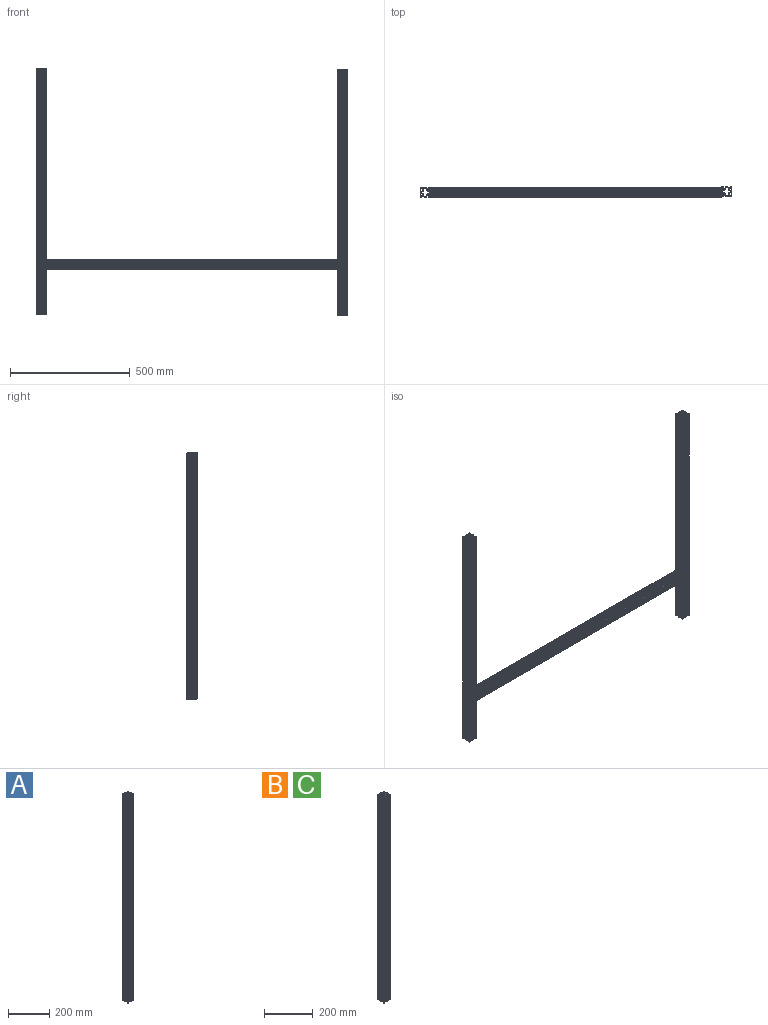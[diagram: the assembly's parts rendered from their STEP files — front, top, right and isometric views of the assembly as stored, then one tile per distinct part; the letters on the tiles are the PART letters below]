
ASSEMBLY  parts=3 mates=2
PART A: 186 faces, bbox 40x40x1220 mm
  f0: plane 1220x1.64mm, normal (0,1,0), area 2000mm2, adj f1,f183,f184,f185
  f1: plane 1220x3.06mm, normal (0.71,0.71,0), area 5280.7mm2, adj f0,f2,f184,f185
  f2: plane 1220x1.95mm, normal (1,0,0), area 2375.6mm2, adj f1,f3,f184,f185
  f3: plane 1220x0.49mm, normal (0.83,0.56,0), area 724.2mm2, adj f2,f4,f184,f185
  f4: plane 1220x0.62mm, normal (0.88,-0.47,0), area 862.7mm2, adj f3,f5,f184,f185
  f5: plane 1220x1.95mm, normal (1,0,0), area 2375.6mm2, adj f4,f6,f184,f185
  f6: plane 1220x3.06mm, normal (0.69,-0.72,0), area 5167.9mm2, adj f5,f7,f184,f185
  f7: plane 1220x1.64mm, normal (0,-1,0), area 2000mm2, adj f6,f8,f184,f185
  f8: plane 1220x2.39mm, normal (-1,0,0), area 2909.7mm2, adj f7,f9,f184,f185
  f9: plane 1220x1.8mm, normal (0.71,-0.71,0), area 3105.6mm2, adj f8,f10,f184,f185
  f10: plane 1220x3.71mm, normal (1,0,0), area 4527.3mm2, adj f9,f11,f184,f185
  f11: cylinder r=1.59mm len=1220mm, axis (0,0,-1), area 4048.6mm2, adj f10,f12,f184,f185
  f12: plane 1220x3.71mm, normal (1,0,0), area 4527.3mm2, adj f11,f13,f184,f185
  f13: plane 1220x1.8mm, normal (0.71,0.71,0), area 3105.6mm2, adj f12,f14,f184,f185
  f14: plane 1220x2.39mm, normal (-1,0,0), area 2909.7mm2, adj f13,f15,f184,f185
  f15: plane 1220x1.64mm, normal (0,1,0), area 2000mm2, adj f14,f16,f184,f185
  f16: plane 1220x3.06mm, normal (0.69,0.72,0), area 5167.9mm2, adj f15,f17,f184,f185
  f17: plane 1220x1.95mm, normal (1,0,0), area 2375.6mm2, adj f16,f18,f184,f185
  f18: plane 1220x0.62mm, normal (0.88,0.47,0), area 862.7mm2, adj f17,f19,f184,f185
  f19: plane 1220x0.49mm, normal (0.83,-0.56,0), area 724.2mm2, adj f18,f20,f184,f185
  f20: plane 1220x1.95mm, normal (1,0,0), area 2375.6mm2, adj f19,f21,f184,f185
  f21: plane 1220x3.06mm, normal (0.71,-0.71,0), area 5280.7mm2, adj f20,f22,f184,f185
  f22: plane 1220x1.64mm, normal (0,-1,0), area 2000mm2, adj f21,f23,f184,f185
  f23: plane 1220x2.39mm, normal (-1,0,0), area 2909.7mm2, adj f22,f24,f184,f185
  f24: plane 1220x1.8mm, normal (0.71,-0.71,0), area 3105.6mm2, adj f23,f25,f184,f185
  f25: plane 1220x1.16mm, normal (1,0,0), area 1416.3mm2, adj f24,f26,f184,f185
  f26: cylinder r=1.59mm len=1220mm, axis (0,0,-1), area 4048.6mm2, adj f25,f27,f184,f185
  f27: plane 1220x0.68mm, normal (1,0,0), area 824.6mm2, adj f26,f28,f184,f185
  f28: cylinder r=0.5mm len=1220mm, axis (0,0,-1), area 958.2mm2, adj f27,f29,f184,f185
  f29: plane 1220x0.68mm, normal (0,1,0), area 824.6mm2, adj f28,f30,f184,f185
  f30: cylinder r=1.59mm len=1220mm, axis (0,0,-1), area 4048.6mm2, adj f29,f31,f184,f185
  f31: plane 1220x1.16mm, normal (0,1,0), area 1416.3mm2, adj f30,f32,f184,f185
  f32: plane 1220x1.8mm, normal (-0.71,0.71,0), area 3105.6mm2, adj f31,f33,f184,f185
  f33: plane 1220x2.39mm, normal (0,-1,0), area 2909.7mm2, adj f32,f34,f184,f185
  f34: plane 1220x1.64mm, normal (-1,0,0), area 2000mm2, adj f33,f35,f184,f185
  f35: plane 1220x3.06mm, normal (-0.71,0.71,0), area 5280.7mm2, adj f34,f36,f184,f185
  f36: plane 1220x1.95mm, normal (0,1,0), area 2375.6mm2, adj f35,f37,f184,f185
  f37: plane 1220x0.49mm, normal (-0.52,0.86,0), area 700.5mm2, adj f36,f38,f184,f185
  f38: plane 1220x0.49mm, normal (0.52,0.86,0), area 700.5mm2, adj f37,f39,f184,f185
  f39: plane 1220x1.95mm, normal (0,1,0), area 2375.6mm2, adj f38,f40,f184,f185
  f40: plane 1220x3.06mm, normal (0.71,0.71,0), area 5280.7mm2, adj f39,f41,f184,f185
  f41: plane 1220x1.64mm, normal (1,0,0), area 2000mm2, adj f40,f42,f184,f185
  f42: plane 1220x2.39mm, normal (0,-1,0), area 2909.7mm2, adj f41,f43,f184,f185
  f43: plane 1220x1.8mm, normal (0.71,0.71,0), area 3105.6mm2, adj f42,f44,f184,f185
  f44: plane 1220x3.71mm, normal (0,1,0), area 4527.3mm2, adj f43,f45,f184,f185
  f45: cylinder r=1.59mm len=1220mm, axis (0,0,-1), area 4048.6mm2, adj f44,f46,f184,f185
  f46: plane 1220x3.71mm, normal (0,1,0), area 4527.3mm2, adj f45,f47,f184,f185
  f47: plane 1220x1.8mm, normal (-0.71,0.71,0), area 3105.6mm2, adj f46,f48,f184,f185
  f48: plane 1220x2.39mm, normal (0,-1,0), area 2909.7mm2, adj f47,f49,f184,f185
  f49: plane 1220x1.64mm, normal (-1,0,0), area 2000mm2, adj f48,f50,f184,f185
  f50: plane 1220x3.06mm, normal (-0.71,0.71,0), area 5280.7mm2, adj f49,f51,f184,f185
  f51: plane 1220x1.95mm, normal (0,1,0), area 2375.6mm2, adj f50,f52,f184,f185
  f52: plane 1220x0.49mm, normal (-0.52,0.86,0), area 700.5mm2, adj f51,f53,f184,f185
  f53: plane 1220x0.49mm, normal (0.52,0.86,0), area 700.5mm2, adj f52,f54,f184,f185
  f54: plane 1220x1.95mm, normal (0,1,0), area 2375.6mm2, adj f53,f55,f184,f185
  f55: plane 1220x3.06mm, normal (0.71,0.71,0), area 5280.7mm2, adj f54,f56,f184,f185
  f56: plane 1220x1.64mm, normal (1,0,0), area 2000mm2, adj f55,f57,f184,f185
  f57: plane 1220x2.39mm, normal (0,-1,0), area 2909.7mm2, adj f56,f58,f184,f185
  f58: plane 1220x1.8mm, normal (0.71,0.71,0), area 3105.6mm2, adj f57,f59,f184,f185
  f59: plane 1220x1.16mm, normal (0,1,0), area 1416.3mm2, adj f58,f60,f184,f185
  f60: cylinder r=1.59mm len=1220mm, axis (0,0,-1), area 4048.6mm2, adj f59,f61,f184,f185
  f61: plane 1220x0.68mm, normal (0,1,0), area 824.6mm2, adj f60,f62,f184,f185
  f62: cylinder r=0.5mm len=1220mm, axis (0,0,-1), area 958.2mm2, adj f61,f63,f184,f185
  f63: plane 1220x0.68mm, normal (-1,0,0), area 824.6mm2, adj f62,f64,f184,f185
  f64: cylinder r=1.59mm len=1220mm, axis (0,0,-1), area 4048.6mm2, adj f63,f65,f184,f185
  f65: plane 1220x1.16mm, normal (-1,0,0), area 1416.3mm2, adj f64,f66,f184,f185
  f66: plane 1220x1.8mm, normal (-0.71,-0.71,0), area 3105.6mm2, adj f65,f67,f184,f185
  f67: plane 1220x2.39mm, normal (1,0,0), area 2909.7mm2, adj f66,f68,f184,f185
  f68: plane 1220x1.64mm, normal (0,-1,0), area 2000mm2, adj f67,f69,f184,f185
  f69: plane 1220x3.06mm, normal (-0.71,-0.71,0), area 5280.7mm2, adj f68,f70,f184,f185
  f70: plane 1220x1.95mm, normal (-1,0,0), area 2375.6mm2, adj f69,f71,f184,f185
  f71: plane 1220x0.49mm, normal (-0.83,-0.56,0), area 724.2mm2, adj f70,f72,f184,f185
  f72: plane 1220x0.62mm, normal (-0.88,0.47,0), area 862.7mm2, adj f71,f73,f184,f185
  f73: plane 1220x1.95mm, normal (-1,0,0), area 2375.6mm2, adj f72,f74,f184,f185
  f74: plane 1220x3.06mm, normal (-0.69,0.72,0), area 5167.9mm2, adj f73,f75,f184,f185
  f75: plane 1220x1.64mm, normal (0,1,0), area 2000mm2, adj f74,f76,f184,f185
  f76: plane 1220x2.39mm, normal (1,0,0), area 2909.7mm2, adj f75,f77,f184,f185
  f77: plane 1220x1.8mm, normal (-0.71,0.71,0), area 3105.6mm2, adj f76,f78,f184,f185
  f78: plane 1220x3.71mm, normal (-1,0,0), area 4527.3mm2, adj f77,f79,f184,f185
  f79: cylinder r=1.59mm len=1220mm, axis (0,0,-1), area 4048.6mm2, adj f78,f80,f184,f185
  f80: plane 1220x3.71mm, normal (-1,0,0), area 4527.3mm2, adj f79,f81,f184,f185
  f81: plane 1220x1.8mm, normal (-0.71,-0.71,0), area 3105.6mm2, adj f80,f82,f184,f185
  f82: plane 1220x2.39mm, normal (1,0,0), area 2909.7mm2, adj f81,f83,f184,f185
  f83: plane 1220x1.64mm, normal (0,-1,0), area 2000mm2, adj f82,f84,f184,f185
  f84: plane 1220x3.06mm, normal (-0.69,-0.72,0), area 5167.9mm2, adj f83,f85,f184,f185
  f85: plane 1220x1.95mm, normal (-1,0,0), area 2375.6mm2, adj f84,f86,f184,f185
  f86: plane 1220x0.62mm, normal (-0.88,-0.47,0), area 862.7mm2, adj f85,f87,f184,f185
  f87: plane 1220x0.49mm, normal (-0.83,0.56,0), area 724.2mm2, adj f86,f88,f184,f185
  f88: plane 1220x1.95mm, normal (-1,0,0), area 2375.6mm2, adj f87,f89,f184,f185
  f89: plane 1220x3.06mm, normal (-0.71,0.71,0), area 5280.7mm2, adj f88,f90,f184,f185
  f90: plane 1220x1.64mm, normal (0,1,0), area 2000mm2, adj f89,f91,f184,f185
  f91: plane 1220x2.39mm, normal (1,0,0), area 2909.7mm2, adj f90,f92,f184,f185
  f92: plane 1220x1.8mm, normal (-0.71,0.71,0), area 3105.6mm2, adj f91,f93,f184,f185
  f93: plane 1220x1.16mm, normal (-1,0,0), area 1416.3mm2, adj f92,f94,f184,f185
  f94: cylinder r=1.59mm len=1220mm, axis (0,0,-1), area 4048.6mm2, adj f93,f95,f184,f185
  f95: plane 1220x0.68mm, normal (-1,0,0), area 824.6mm2, adj f94,f96,f184,f185
  f96: cylinder r=0.5mm len=1220mm, axis (0,0,-1), area 958.2mm2, adj f95,f97,f184,f185
  f97: plane 1220x0.68mm, normal (0,-1,0), area 824.6mm2, adj f96,f98,f184,f185
  f98: cylinder r=1.59mm len=1220mm, axis (0,0,-1), area 4048.6mm2, adj f97,f99,f184,f185
  f99: plane 1220x1.16mm, normal (0,-1,0), area 1416.3mm2, adj f98,f100,f184,f185
  f100: plane 1220x1.8mm, normal (0.71,-0.71,0), area 3105.6mm2, adj f99,f101,f184,f185
  f101: plane 1220x2.39mm, normal (0,1,0), area 2909.7mm2, adj f100,f102,f184,f185
  f102: plane 1220x1.64mm, normal (1,0,0), area 2000mm2, adj f101,f103,f184,f185
  f103: plane 1220x3.06mm, normal (0.71,-0.71,0), area 5280.7mm2, adj f102,f104,f184,f185
  f104: plane 1220x1.95mm, normal (0,-1,0), area 2375.6mm2, adj f103,f105,f184,f185
  f105: plane 1220x0.49mm, normal (0.52,-0.86,0), area 700.5mm2, adj f104,f106,f184,f185
  f106: plane 1220x0.49mm, normal (-0.52,-0.86,0), area 700.5mm2, adj f105,f107,f184,f185
  f107: plane 1220x1.95mm, normal (0,-1,0), area 2375.6mm2, adj f106,f108,f184,f185
  f108: plane 1220x3.06mm, normal (-0.71,-0.71,0), area 5280.7mm2, adj f107,f109,f184,f185
  f109: plane 1220x1.64mm, normal (-1,0,0), area 2000mm2, adj f108,f110,f184,f185
  f110: plane 1220x2.39mm, normal (0,1,0), area 2909.7mm2, adj f109,f111,f184,f185
  f111: plane 1220x1.8mm, normal (-0.71,-0.71,0), area 3105.6mm2, adj f110,f112,f184,f185
  f112: plane 1220x3.71mm, normal (0,-1,0), area 4527.3mm2, adj f111,f113,f184,f185
  f113: cylinder r=1.59mm len=1220mm, axis (0,0,-1), area 4048.6mm2, adj f112,f114,f184,f185
  f114: plane 1220x3.71mm, normal (0,-1,0), area 4527.3mm2, adj f113,f115,f184,f185
  f115: plane 1220x1.8mm, normal (0.71,-0.71,0), area 3105.6mm2, adj f114,f116,f184,f185
  f116: plane 1220x2.39mm, normal (0,1,0), area 2909.7mm2, adj f115,f117,f184,f185
  f117: plane 1220x1.64mm, normal (1,0,0), area 2000mm2, adj f116,f118,f184,f185
  f118: plane 1220x3.06mm, normal (0.71,-0.71,0), area 5280.7mm2, adj f117,f119,f184,f185
  f119: plane 1220x1.95mm, normal (0,-1,0), area 2375.6mm2, adj f118,f120,f184,f185
  f120: plane 1220x0.49mm, normal (0.52,-0.86,0), area 700.5mm2, adj f119,f121,f184,f185
  f121: plane 1220x0.49mm, normal (-0.52,-0.86,0), area 700.5mm2, adj f120,f122,f184,f185
  f122: plane 1220x1.95mm, normal (0,-1,0), area 2375.6mm2, adj f121,f123,f184,f185
  f123: plane 1220x3.06mm, normal (-0.71,-0.71,0), area 5280.7mm2, adj f122,f124,f184,f185
  f124: plane 1220x1.64mm, normal (-1,0,0), area 2000mm2, adj f123,f125,f184,f185
  f125: plane 1220x2.39mm, normal (0,1,0), area 2909.7mm2, adj f124,f126,f184,f185
  f126: plane 1220x1.8mm, normal (-0.71,-0.71,0), area 3105.6mm2, adj f125,f127,f184,f185
  f127: plane 1220x1.16mm, normal (0,-1,0), area 1416.3mm2, adj f126,f128,f184,f185
  f128: cylinder r=1.59mm len=1220mm, axis (0,0,-1), area 4048.6mm2, adj f127,f129,f184,f185
  f129: plane 1220x0.68mm, normal (0,-1,0), area 824.6mm2, adj f128,f130,f184,f185
  f130: cylinder r=0.5mm len=1220mm, axis (0,0,-1), area 958.2mm2, adj f129,f131,f184,f185
  f131: plane 1220x0.68mm, normal (1,0,0), area 824.6mm2, adj f130,f132,f184,f185
  f132: cylinder r=1.59mm len=1220mm, axis (0,0,-1), area 4048.6mm2, adj f131,f133,f184,f185
  f133: plane 1220x1.16mm, normal (1,0,0), area 1416.3mm2, adj f132,f134,f184,f185
  f134: plane 1220x1.8mm, normal (0.71,0.71,0), area 3105.6mm2, adj f133,f183,f184,f185
  f135: cylinder r=2.1mm len=1220mm, axis (0,0,-1), area 14264.2mm2, adj f136,f182,f184,f185
  f136: plane 1220x1.59mm, normal (0,1,0), area 1938.7mm2, adj f135,f137,f184,f185
  f137: plane 1220x3.31mm, normal (-1,0,0), area 4038.4mm2, adj f136,f138,f184,f185
  f138: plane 1220x3.8mm, normal (-0.71,0.71,0), area 6556.3mm2, adj f137,f139,f184,f185
  f139: plane 1220x1.96mm, normal (-1,0,0), area 2392mm2, adj f138,f140,f184,f185
  f140: plane 1220x0.52mm, normal (0,1,0), area 640.1mm2, adj f139,f141,f184,f185
  f141: cylinder r=3.39mm len=1220mm, axis (0,0,-1), area 5762.9mm2, adj f140,f142,f184,f185
  f142: plane 1220x0.52mm, normal (0,1,0), area 640.1mm2, adj f141,f143,f184,f185
  f143: plane 1220x1.96mm, normal (1,0,0), area 2392mm2, adj f142,f144,f184,f185
  f144: plane 1220x3.8mm, normal (0.71,0.71,0), area 6556.3mm2, adj f143,f145,f184,f185
  f145: plane 1220x3.31mm, normal (1,0,0), area 4038.4mm2, adj f144,f146,f184,f185
  f146: plane 1220x1.59mm, normal (0,1,0), area 1938.7mm2, adj f145,f147,f184,f185
  f147: cylinder r=2.1mm len=1220mm, axis (0,0,-1), area 14264.2mm2, adj f146,f148,f184,f185
  f148: plane 1220x1.59mm, normal (1,0,0), area 1938.7mm2, adj f147,f149,f184,f185
  f149: plane 1220x3.17mm, normal (0,1,0), area 3869.3mm2, adj f148,f150,f184,f185
  f150: plane 1220x3.97mm, normal (0.69,0.72,0), area 6705.9mm2, adj f149,f151,f184,f185
  f151: plane 1220x1.93mm, normal (0,1,0), area 2351.9mm2, adj f150,f152,f184,f185
  f152: plane 1220x0.52mm, normal (1,0,0), area 640.1mm2, adj f151,f153,f184,f185
  f153: cylinder r=3.39mm len=1220mm, axis (0,0,-1), area 5762.9mm2, adj f152,f154,f184,f185
  f154: plane 1220x0.52mm, normal (1,0,0), area 640.1mm2, adj f153,f155,f184,f185
  f155: plane 1220x1.93mm, normal (0,-1,0), area 2351.9mm2, adj f154,f156,f184,f185
  f156: plane 1220x3.97mm, normal (0.69,-0.72,0), area 6705.9mm2, adj f155,f157,f184,f185
  f157: plane 1220x3.17mm, normal (0,-1,0), area 3869.3mm2, adj f156,f158,f184,f185
  f158: plane 1220x1.59mm, normal (1,0,0), area 1938.7mm2, adj f157,f159,f184,f185
  f159: cylinder r=2.1mm len=1220mm, axis (0,0,-1), area 14264.2mm2, adj f158,f160,f184,f185
  f160: plane 1220x1.59mm, normal (0,-1,0), area 1938.7mm2, adj f159,f161,f184,f185
  f161: plane 1220x3.31mm, normal (1,0,0), area 4038.4mm2, adj f160,f162,f184,f185
  f162: plane 1220x3.8mm, normal (0.71,-0.71,0), area 6556.3mm2, adj f161,f163,f184,f185
  f163: plane 1220x1.96mm, normal (1,0,0), area 2392mm2, adj f162,f164,f184,f185
  f164: plane 1220x0.52mm, normal (0,-1,0), area 640.1mm2, adj f163,f165,f184,f185
  f165: cylinder r=3.39mm len=1220mm, axis (0,0,-1), area 5762.9mm2, adj f164,f166,f184,f185
  f166: plane 1220x0.52mm, normal (0,-1,0), area 640.1mm2, adj f165,f167,f184,f185
  f167: plane 1220x1.96mm, normal (-1,0,0), area 2392mm2, adj f166,f168,f184,f185
  f168: plane 1220x3.8mm, normal (-0.71,-0.71,0), area 6556.3mm2, adj f167,f169,f184,f185
  f169: plane 1220x3.31mm, normal (-1,0,0), area 4038.4mm2, adj f168,f170,f184,f185
  f170: plane 1220x1.59mm, normal (0,-1,0), area 1938.7mm2, adj f169,f171,f184,f185
  f171: cylinder r=2.1mm len=1220mm, axis (0,0,-1), area 14264.2mm2, adj f170,f172,f184,f185
  f172: plane 1220x1.59mm, normal (-1,0,0), area 1938.7mm2, adj f171,f173,f184,f185
  f173: plane 1220x3.17mm, normal (0,-1,0), area 3869.3mm2, adj f172,f174,f184,f185
  f174: plane 1220x3.97mm, normal (-0.69,-0.72,0), area 6705.9mm2, adj f173,f175,f184,f185
  f175: plane 1220x1.93mm, normal (0,-1,0), area 2351.9mm2, adj f174,f176,f184,f185
  f176: plane 1220x0.52mm, normal (-1,0,0), area 640.1mm2, adj f175,f177,f184,f185
  f177: cylinder r=3.39mm len=1220mm, axis (0,0,-1), area 5762.9mm2, adj f176,f178,f184,f185
  f178: plane 1220x0.52mm, normal (-1,0,0), area 640.1mm2, adj f177,f179,f184,f185
  f179: plane 1220x1.93mm, normal (0,1,0), area 2351.9mm2, adj f178,f180,f184,f185
  f180: plane 1220x3.97mm, normal (-0.69,0.72,0), area 6705.9mm2, adj f179,f181,f184,f185
  f181: plane 1220x3.17mm, normal (0,1,0), area 3869.3mm2, adj f180,f182,f184,f185
  f182: plane 1220x1.59mm, normal (-1,0,0), area 1938.7mm2, adj f135,f181,f184,f185
  f183: plane 1220x2.39mm, normal (-1,0,0), area 2909.7mm2, adj f0,f134,f184,f185
  f184: plane 40x40mm, normal (0,0,1), area 394.7mm2, adj f0,f1,f2,f3,f4,f5,f6,f7
  f185: plane 40x40mm, normal (0,0,-1), area 394.7mm2, adj f0,f1,f2,f3,f4,f5,f6,f7
PART B: 186 faces, bbox 40x40x1030 mm
  f0: plane 1030x1.64mm, normal (0,1,0), area 1688.5mm2, adj f1,f183,f184,f185
  f1: plane 1030x3.06mm, normal (0.71,0.71,0), area 4458.3mm2, adj f0,f2,f184,f185
  f2: plane 1030x1.95mm, normal (1,0,0), area 2005.6mm2, adj f1,f3,f184,f185
  f3: plane 1030x0.49mm, normal (0.83,0.56,0), area 611.5mm2, adj f2,f4,f184,f185
  f4: plane 1030x0.62mm, normal (0.88,-0.47,0), area 728.3mm2, adj f3,f5,f184,f185
  f5: plane 1030x1.95mm, normal (1,0,0), area 2005.6mm2, adj f4,f6,f184,f185
  f6: plane 1030x3.06mm, normal (0.69,-0.72,0), area 4363.1mm2, adj f5,f7,f184,f185
  f7: plane 1030x1.64mm, normal (0,-1,0), area 1688.5mm2, adj f6,f8,f184,f185
  f8: plane 1030x2.39mm, normal (-1,0,0), area 2456.6mm2, adj f7,f9,f184,f185
  f9: plane 1030x1.8mm, normal (0.71,-0.71,0), area 2622mm2, adj f8,f10,f184,f185
  f10: plane 1030x3.71mm, normal (1,0,0), area 3822.2mm2, adj f9,f11,f184,f185
  f11: cylinder r=1.59mm len=1030mm, axis (0,0,-1), area 3418.1mm2, adj f10,f12,f184,f185
  f12: plane 1030x3.71mm, normal (1,0,0), area 3822.2mm2, adj f11,f13,f184,f185
  f13: plane 1030x1.8mm, normal (0.71,0.71,0), area 2622mm2, adj f12,f14,f184,f185
  f14: plane 1030x2.39mm, normal (-1,0,0), area 2456.5mm2, adj f13,f15,f184,f185
  f15: plane 1030x1.64mm, normal (0,1,0), area 1688.5mm2, adj f14,f16,f184,f185
  f16: plane 1030x3.06mm, normal (0.69,0.72,0), area 4363.1mm2, adj f15,f17,f184,f185
  f17: plane 1030x1.95mm, normal (1,0,0), area 2005.6mm2, adj f16,f18,f184,f185
  f18: plane 1030x0.62mm, normal (0.88,0.47,0), area 728.3mm2, adj f17,f19,f184,f185
  f19: plane 1030x0.49mm, normal (0.83,-0.56,0), area 611.5mm2, adj f18,f20,f184,f185
  f20: plane 1030x1.95mm, normal (1,0,0), area 2005.6mm2, adj f19,f21,f184,f185
  f21: plane 1030x3.06mm, normal (0.71,-0.71,0), area 4458.3mm2, adj f20,f22,f184,f185
  f22: plane 1030x1.64mm, normal (0,-1,0), area 1688.5mm2, adj f21,f23,f184,f185
  f23: plane 1030x2.39mm, normal (-1,0,0), area 2456.6mm2, adj f22,f24,f184,f185
  f24: plane 1030x1.8mm, normal (0.71,-0.71,0), area 2622mm2, adj f23,f25,f184,f185
  f25: plane 1030x1.16mm, normal (1,0,0), area 1195.7mm2, adj f24,f26,f184,f185
  f26: cylinder r=1.59mm len=1030mm, axis (0,0,-1), area 3418.1mm2, adj f25,f27,f184,f185
  f27: plane 1030x0.68mm, normal (1,0,0), area 696.2mm2, adj f26,f28,f184,f185
  f28: cylinder r=0.5mm len=1030mm, axis (0,0,-1), area 809mm2, adj f27,f29,f184,f185
  f29: plane 1030x0.68mm, normal (0,1,0), area 696.2mm2, adj f28,f30,f184,f185
  f30: cylinder r=1.59mm len=1030mm, axis (0,0,-1), area 3418.1mm2, adj f29,f31,f184,f185
  f31: plane 1030x1.16mm, normal (0,1,0), area 1195.7mm2, adj f30,f32,f184,f185
  f32: plane 1030x1.8mm, normal (-0.71,0.71,0), area 2622mm2, adj f31,f33,f184,f185
  f33: plane 1030x2.39mm, normal (0,-1,0), area 2456.5mm2, adj f32,f34,f184,f185
  f34: plane 1030x1.64mm, normal (-1,0,0), area 1688.5mm2, adj f33,f35,f184,f185
  f35: plane 1030x3.06mm, normal (-0.71,0.71,0), area 4458.3mm2, adj f34,f36,f184,f185
  f36: plane 1030x1.95mm, normal (0,1,0), area 2005.6mm2, adj f35,f37,f184,f185
  f37: plane 1030x0.49mm, normal (-0.52,0.86,0), area 591.4mm2, adj f36,f38,f184,f185
  f38: plane 1030x0.49mm, normal (0.52,0.86,0), area 591.4mm2, adj f37,f39,f184,f185
  f39: plane 1030x1.95mm, normal (0,1,0), area 2005.6mm2, adj f38,f40,f184,f185
  f40: plane 1030x3.06mm, normal (0.71,0.71,0), area 4458.3mm2, adj f39,f41,f184,f185
  f41: plane 1030x1.64mm, normal (1,0,0), area 1688.5mm2, adj f40,f42,f184,f185
  f42: plane 1030x2.39mm, normal (0,-1,0), area 2456.6mm2, adj f41,f43,f184,f185
  f43: plane 1030x1.8mm, normal (0.71,0.71,0), area 2622mm2, adj f42,f44,f184,f185
  f44: plane 1030x3.71mm, normal (0,1,0), area 3822.2mm2, adj f43,f45,f184,f185
  f45: cylinder r=1.59mm len=1030mm, axis (0,0,-1), area 3418.1mm2, adj f44,f46,f184,f185
  f46: plane 1030x3.71mm, normal (0,1,0), area 3822.2mm2, adj f45,f47,f184,f185
  f47: plane 1030x1.8mm, normal (-0.71,0.71,0), area 2622mm2, adj f46,f48,f184,f185
  f48: plane 1030x2.39mm, normal (0,-1,0), area 2456.6mm2, adj f47,f49,f184,f185
  f49: plane 1030x1.64mm, normal (-1,0,0), area 1688.5mm2, adj f48,f50,f184,f185
  f50: plane 1030x3.06mm, normal (-0.71,0.71,0), area 4458.3mm2, adj f49,f51,f184,f185
  f51: plane 1030x1.95mm, normal (0,1,0), area 2005.6mm2, adj f50,f52,f184,f185
  f52: plane 1030x0.49mm, normal (-0.52,0.86,0), area 591.4mm2, adj f51,f53,f184,f185
  f53: plane 1030x0.49mm, normal (0.52,0.86,0), area 591.4mm2, adj f52,f54,f184,f185
  f54: plane 1030x1.95mm, normal (0,1,0), area 2005.6mm2, adj f53,f55,f184,f185
  f55: plane 1030x3.06mm, normal (0.71,0.71,0), area 4458.3mm2, adj f54,f56,f184,f185
  f56: plane 1030x1.64mm, normal (1,0,0), area 1688.5mm2, adj f55,f57,f184,f185
  f57: plane 1030x2.39mm, normal (0,-1,0), area 2456.5mm2, adj f56,f58,f184,f185
  f58: plane 1030x1.8mm, normal (0.71,0.71,0), area 2622mm2, adj f57,f59,f184,f185
  f59: plane 1030x1.16mm, normal (0,1,0), area 1195.7mm2, adj f58,f60,f184,f185
  f60: cylinder r=1.59mm len=1030mm, axis (0,0,-1), area 3418.1mm2, adj f59,f61,f184,f185
  f61: plane 1030x0.68mm, normal (0,1,0), area 696.2mm2, adj f60,f62,f184,f185
  f62: cylinder r=0.5mm len=1030mm, axis (0,0,-1), area 809mm2, adj f61,f63,f184,f185
  f63: plane 1030x0.68mm, normal (-1,0,0), area 696.2mm2, adj f62,f64,f184,f185
  f64: cylinder r=1.59mm len=1030mm, axis (0,0,-1), area 3418.1mm2, adj f63,f65,f184,f185
  f65: plane 1030x1.16mm, normal (-1,0,0), area 1195.7mm2, adj f64,f66,f184,f185
  f66: plane 1030x1.8mm, normal (-0.71,-0.71,0), area 2622mm2, adj f65,f67,f184,f185
  f67: plane 1030x2.39mm, normal (1,0,0), area 2456.6mm2, adj f66,f68,f184,f185
  f68: plane 1030x1.64mm, normal (0,-1,0), area 1688.5mm2, adj f67,f69,f184,f185
  f69: plane 1030x3.06mm, normal (-0.71,-0.71,0), area 4458.3mm2, adj f68,f70,f184,f185
  f70: plane 1030x1.95mm, normal (-1,0,0), area 2005.6mm2, adj f69,f71,f184,f185
  f71: plane 1030x0.49mm, normal (-0.83,-0.56,0), area 611.5mm2, adj f70,f72,f184,f185
  f72: plane 1030x0.62mm, normal (-0.88,0.47,0), area 728.3mm2, adj f71,f73,f184,f185
  f73: plane 1030x1.95mm, normal (-1,0,0), area 2005.6mm2, adj f72,f74,f184,f185
  f74: plane 1030x3.06mm, normal (-0.69,0.72,0), area 4363.1mm2, adj f73,f75,f184,f185
  f75: plane 1030x1.64mm, normal (0,1,0), area 1688.5mm2, adj f74,f76,f184,f185
  f76: plane 1030x2.39mm, normal (1,0,0), area 2456.5mm2, adj f75,f77,f184,f185
  f77: plane 1030x1.8mm, normal (-0.71,0.71,0), area 2622mm2, adj f76,f78,f184,f185
  f78: plane 1030x3.71mm, normal (-1,0,0), area 3822.2mm2, adj f77,f79,f184,f185
  f79: cylinder r=1.59mm len=1030mm, axis (0,0,-1), area 3418.1mm2, adj f78,f80,f184,f185
  f80: plane 1030x3.71mm, normal (-1,0,0), area 3822.2mm2, adj f79,f81,f184,f185
  f81: plane 1030x1.8mm, normal (-0.71,-0.71,0), area 2622mm2, adj f80,f82,f184,f185
  f82: plane 1030x2.39mm, normal (1,0,0), area 2456.6mm2, adj f81,f83,f184,f185
  f83: plane 1030x1.64mm, normal (0,-1,0), area 1688.5mm2, adj f82,f84,f184,f185
  f84: plane 1030x3.06mm, normal (-0.69,-0.72,0), area 4363.1mm2, adj f83,f85,f184,f185
  f85: plane 1030x1.95mm, normal (-1,0,0), area 2005.6mm2, adj f84,f86,f184,f185
  f86: plane 1030x0.62mm, normal (-0.88,-0.47,0), area 728.3mm2, adj f85,f87,f184,f185
  f87: plane 1030x0.49mm, normal (-0.83,0.56,0), area 611.5mm2, adj f86,f88,f184,f185
  f88: plane 1030x1.95mm, normal (-1,0,0), area 2005.6mm2, adj f87,f89,f184,f185
  f89: plane 1030x3.06mm, normal (-0.71,0.71,0), area 4458.3mm2, adj f88,f90,f184,f185
  f90: plane 1030x1.64mm, normal (0,1,0), area 1688.5mm2, adj f89,f91,f184,f185
  f91: plane 1030x2.39mm, normal (1,0,0), area 2456.6mm2, adj f90,f92,f184,f185
  f92: plane 1030x1.8mm, normal (-0.71,0.71,0), area 2622mm2, adj f91,f93,f184,f185
  f93: plane 1030x1.16mm, normal (-1,0,0), area 1195.7mm2, adj f92,f94,f184,f185
  f94: cylinder r=1.59mm len=1030mm, axis (0,0,-1), area 3418.1mm2, adj f93,f95,f184,f185
  f95: plane 1030x0.68mm, normal (-1,0,0), area 696.2mm2, adj f94,f96,f184,f185
  f96: cylinder r=0.5mm len=1030mm, axis (0,0,-1), area 809mm2, adj f95,f97,f184,f185
  f97: plane 1030x0.68mm, normal (0,-1,0), area 696.2mm2, adj f96,f98,f184,f185
  f98: cylinder r=1.59mm len=1030mm, axis (0,0,-1), area 3418.1mm2, adj f97,f99,f184,f185
  f99: plane 1030x1.16mm, normal (0,-1,0), area 1195.7mm2, adj f98,f100,f184,f185
  f100: plane 1030x1.8mm, normal (0.71,-0.71,0), area 2622mm2, adj f99,f101,f184,f185
  f101: plane 1030x2.39mm, normal (0,1,0), area 2456.6mm2, adj f100,f102,f184,f185
  f102: plane 1030x1.64mm, normal (1,0,0), area 1688.5mm2, adj f101,f103,f184,f185
  f103: plane 1030x3.06mm, normal (0.71,-0.71,0), area 4458.3mm2, adj f102,f104,f184,f185
  f104: plane 1030x1.95mm, normal (0,-1,0), area 2005.6mm2, adj f103,f105,f184,f185
  f105: plane 1030x0.49mm, normal (0.52,-0.86,0), area 591.4mm2, adj f104,f106,f184,f185
  f106: plane 1030x0.49mm, normal (-0.52,-0.86,0), area 591.4mm2, adj f105,f107,f184,f185
  f107: plane 1030x1.95mm, normal (0,-1,0), area 2005.6mm2, adj f106,f108,f184,f185
  f108: plane 1030x3.06mm, normal (-0.71,-0.71,0), area 4458.3mm2, adj f107,f109,f184,f185
  f109: plane 1030x1.64mm, normal (-1,0,0), area 1688.5mm2, adj f108,f110,f184,f185
  f110: plane 1030x2.39mm, normal (0,1,0), area 2456.6mm2, adj f109,f111,f184,f185
  f111: plane 1030x1.8mm, normal (-0.71,-0.71,0), area 2622mm2, adj f110,f112,f184,f185
  f112: plane 1030x3.71mm, normal (0,-1,0), area 3822.2mm2, adj f111,f113,f184,f185
  f113: cylinder r=1.59mm len=1030mm, axis (0,0,-1), area 3418.1mm2, adj f112,f114,f184,f185
  f114: plane 1030x3.71mm, normal (0,-1,0), area 3822.2mm2, adj f113,f115,f184,f185
  f115: plane 1030x1.8mm, normal (0.71,-0.71,0), area 2622mm2, adj f114,f116,f184,f185
  f116: plane 1030x2.39mm, normal (0,1,0), area 2456.6mm2, adj f115,f117,f184,f185
  f117: plane 1030x1.64mm, normal (1,0,0), area 1688.5mm2, adj f116,f118,f184,f185
  f118: plane 1030x3.06mm, normal (0.71,-0.71,0), area 4458.3mm2, adj f117,f119,f184,f185
  f119: plane 1030x1.95mm, normal (0,-1,0), area 2005.6mm2, adj f118,f120,f184,f185
  f120: plane 1030x0.49mm, normal (0.52,-0.86,0), area 591.4mm2, adj f119,f121,f184,f185
  f121: plane 1030x0.49mm, normal (-0.52,-0.86,0), area 591.4mm2, adj f120,f122,f184,f185
  f122: plane 1030x1.95mm, normal (0,-1,0), area 2005.6mm2, adj f121,f123,f184,f185
  f123: plane 1030x3.06mm, normal (-0.71,-0.71,0), area 4458.3mm2, adj f122,f124,f184,f185
  f124: plane 1030x1.64mm, normal (-1,0,0), area 1688.5mm2, adj f123,f125,f184,f185
  f125: plane 1030x2.39mm, normal (0,1,0), area 2456.6mm2, adj f124,f126,f184,f185
  f126: plane 1030x1.8mm, normal (-0.71,-0.71,0), area 2622mm2, adj f125,f127,f184,f185
  f127: plane 1030x1.16mm, normal (0,-1,0), area 1195.7mm2, adj f126,f128,f184,f185
  f128: cylinder r=1.59mm len=1030mm, axis (0,0,-1), area 3418.1mm2, adj f127,f129,f184,f185
  f129: plane 1030x0.68mm, normal (0,-1,0), area 696.2mm2, adj f128,f130,f184,f185
  f130: cylinder r=0.5mm len=1030mm, axis (0,0,-1), area 809mm2, adj f129,f131,f184,f185
  f131: plane 1030x0.68mm, normal (1,0,0), area 696.2mm2, adj f130,f132,f184,f185
  f132: cylinder r=1.59mm len=1030mm, axis (0,0,-1), area 3418.1mm2, adj f131,f133,f184,f185
  f133: plane 1030x1.16mm, normal (1,0,0), area 1195.7mm2, adj f132,f134,f184,f185
  f134: plane 1030x1.8mm, normal (0.71,0.71,0), area 2622mm2, adj f133,f183,f184,f185
  f135: cylinder r=2.1mm len=1030mm, axis (0,0,-1), area 12042.7mm2, adj f136,f182,f184,f185
  f136: plane 1030x1.59mm, normal (0,1,0), area 1636.8mm2, adj f135,f137,f184,f185
  f137: plane 1030x3.31mm, normal (-1,0,0), area 3409.5mm2, adj f136,f138,f184,f185
  f138: plane 1030x3.8mm, normal (-0.71,0.71,0), area 5535.2mm2, adj f137,f139,f184,f185
  f139: plane 1030x1.96mm, normal (-1,0,0), area 2019.5mm2, adj f138,f140,f184,f185
  f140: plane 1030x0.52mm, normal (0,1,0), area 540.4mm2, adj f139,f141,f184,f185
  f141: cylinder r=3.39mm len=1030mm, axis (0,0,-1), area 4865.4mm2, adj f140,f142,f184,f185
  f142: plane 1030x0.52mm, normal (0,1,0), area 540.4mm2, adj f141,f143,f184,f185
  f143: plane 1030x1.96mm, normal (1,0,0), area 2019.5mm2, adj f142,f144,f184,f185
  f144: plane 1030x3.8mm, normal (0.71,0.71,0), area 5535.2mm2, adj f143,f145,f184,f185
  f145: plane 1030x3.31mm, normal (1,0,0), area 3409.5mm2, adj f144,f146,f184,f185
  f146: plane 1030x1.59mm, normal (0,1,0), area 1636.8mm2, adj f145,f147,f184,f185
  f147: cylinder r=2.1mm len=1030mm, axis (0,0,-1), area 12042.7mm2, adj f146,f148,f184,f185
  f148: plane 1030x1.59mm, normal (1,0,0), area 1636.8mm2, adj f147,f149,f184,f185
  f149: plane 1030x3.17mm, normal (0,1,0), area 3266.7mm2, adj f148,f150,f184,f185
  f150: plane 1030x3.97mm, normal (0.69,0.72,0), area 5661.5mm2, adj f149,f151,f184,f185
  f151: plane 1030x1.93mm, normal (0,1,0), area 1985.7mm2, adj f150,f152,f184,f185
  f152: plane 1030x0.52mm, normal (1,0,0), area 540.4mm2, adj f151,f153,f184,f185
  f153: cylinder r=3.39mm len=1030mm, axis (0,0,-1), area 4865.4mm2, adj f152,f154,f184,f185
  f154: plane 1030x0.52mm, normal (1,0,0), area 540.4mm2, adj f153,f155,f184,f185
  f155: plane 1030x1.93mm, normal (0,-1,0), area 1985.7mm2, adj f154,f156,f184,f185
  f156: plane 1030x3.97mm, normal (0.69,-0.72,0), area 5661.5mm2, adj f155,f157,f184,f185
  f157: plane 1030x3.17mm, normal (0,-1,0), area 3266.7mm2, adj f156,f158,f184,f185
  f158: plane 1030x1.59mm, normal (1,0,0), area 1636.8mm2, adj f157,f159,f184,f185
  f159: cylinder r=2.1mm len=1030mm, axis (0,0,-1), area 12042.7mm2, adj f158,f160,f184,f185
  f160: plane 1030x1.59mm, normal (0,-1,0), area 1636.8mm2, adj f159,f161,f184,f185
  f161: plane 1030x3.31mm, normal (1,0,0), area 3409.5mm2, adj f160,f162,f184,f185
  f162: plane 1030x3.8mm, normal (0.71,-0.71,0), area 5535.2mm2, adj f161,f163,f184,f185
  f163: plane 1030x1.96mm, normal (1,0,0), area 2019.5mm2, adj f162,f164,f184,f185
  f164: plane 1030x0.52mm, normal (0,-1,0), area 540.4mm2, adj f163,f165,f184,f185
  f165: cylinder r=3.39mm len=1030mm, axis (0,0,-1), area 4865.4mm2, adj f164,f166,f184,f185
  f166: plane 1030x0.52mm, normal (0,-1,0), area 540.4mm2, adj f165,f167,f184,f185
  f167: plane 1030x1.96mm, normal (-1,0,0), area 2019.5mm2, adj f166,f168,f184,f185
  f168: plane 1030x3.8mm, normal (-0.71,-0.71,0), area 5535.2mm2, adj f167,f169,f184,f185
  f169: plane 1030x3.31mm, normal (-1,0,0), area 3409.5mm2, adj f168,f170,f184,f185
  f170: plane 1030x1.59mm, normal (0,-1,0), area 1636.8mm2, adj f169,f171,f184,f185
  f171: cylinder r=2.1mm len=1030mm, axis (0,0,-1), area 12042.7mm2, adj f170,f172,f184,f185
  f172: plane 1030x1.59mm, normal (-1,0,0), area 1636.8mm2, adj f171,f173,f184,f185
  f173: plane 1030x3.17mm, normal (0,-1,0), area 3266.7mm2, adj f172,f174,f184,f185
  f174: plane 1030x3.97mm, normal (-0.69,-0.72,0), area 5661.5mm2, adj f173,f175,f184,f185
  f175: plane 1030x1.93mm, normal (0,-1,0), area 1985.7mm2, adj f174,f176,f184,f185
  f176: plane 1030x0.52mm, normal (-1,0,0), area 540.4mm2, adj f175,f177,f184,f185
  f177: cylinder r=3.39mm len=1030mm, axis (0,0,-1), area 4865.4mm2, adj f176,f178,f184,f185
  f178: plane 1030x0.52mm, normal (-1,0,0), area 540.4mm2, adj f177,f179,f184,f185
  f179: plane 1030x1.93mm, normal (0,1,0), area 1985.7mm2, adj f178,f180,f184,f185
  f180: plane 1030x3.97mm, normal (-0.69,0.72,0), area 5661.5mm2, adj f179,f181,f184,f185
  f181: plane 1030x3.17mm, normal (0,1,0), area 3266.7mm2, adj f180,f182,f184,f185
  f182: plane 1030x1.59mm, normal (-1,0,0), area 1636.8mm2, adj f135,f181,f184,f185
  f183: plane 1030x2.39mm, normal (-1,0,0), area 2456.6mm2, adj f0,f134,f184,f185
  f184: plane 40x40mm, normal (0,0,1), area 394.7mm2, adj f0,f1,f2,f3,f4,f5,f6,f7
  f185: plane 40x40mm, normal (0,0,-1), area 394.7mm2, adj f0,f1,f2,f3,f4,f5,f6,f7
PART C: same geometry as B
PLACE A rot(axis=(0.71,0,0.71),180deg) t=(1685.56,302.95,604.9)mm
PLACE B t=(1667.33,302.95,393.13)mm fixed
PLACE C rot(axis=(0,0,-1),90deg) t=(2925.56,306.18,389.9)mm
MATE fastened C.f114 <-> A.f184  axis (-1,0,0) through (2905.56,302.95,904.9)mm
MATE fastened A.f114 <-> B.f29  axis (0,1,0) through (1685.56,322.95,608.13)mm
